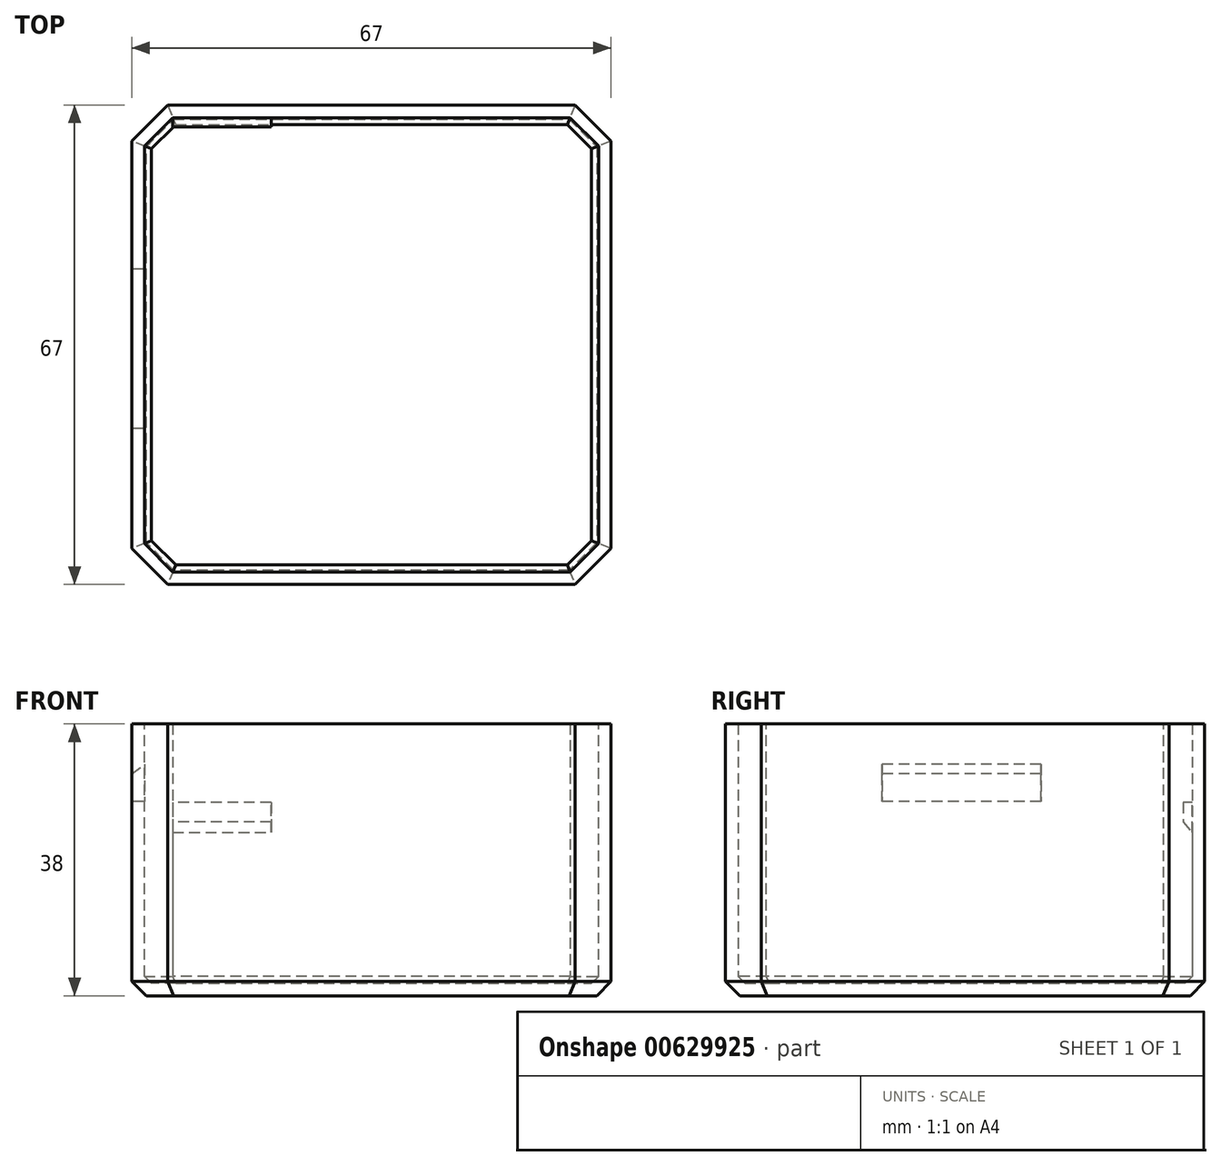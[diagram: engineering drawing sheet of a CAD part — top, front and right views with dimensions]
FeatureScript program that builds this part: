
annotation { "Feature Type Name" : "Feature", "Feature Type Description" : "" }
export const myFeature = defineFeature(function(context is Context, id is Id, definition is map)
    precondition{}
    {
        {
            var Q0;
            Q0=qCreatedBy(makeId("Top.planeOp"),FACE);
            var sketch = newSketch(context, id + "F0", { "sketchPlane" : qUnion([Q0])});
            skLineSegment(sketch, "E0.bottom", {"start": v(0, 0) * mm, "end": v(67, 0) * mm});
            skLineSegment(sketch, "E0.top", {"start": v(0, 67) * mm, "end": v(67, 67) * mm});
            skLineSegment(sketch, "E0.left", {"start": v(0, 0) * mm, "end": v(0, 67) * mm});
            skLineSegment(sketch, "E0.right", {"start": v(67, 0) * mm, "end": v(67, 67) * mm});
            skSolve(sketch);
        }
        {
            var Q0;
            Q0=makeQuery(id+"F0.imprint","IMPRINT",FACE,{"disambiguationData":[TD([[makeQuery(id+"F0.imprint","IMPRINT",EDGE,{"derivedFrom":sQuery(id+"F0.wireOp",EDGE,"E0.bottom")}),1.0]])]});
            extrude(context, id + "F1", {"entities" : qUnion([Q0]), "depth" : 38 * mm, "offsetDistance" : 25 * mm});
        }
        {
            var Q0;
            Q0=makeQuery(id+"F1.opExtrude","SWEPT_EDGE",EDGE,{"disambiguationData":[OSD([sQuery(id+"F0.wireOp",EDGE,"E0.top"),sQuery(id+"F0.wireOp",EDGE,"E0.right")])]});
            var Q1;
            Q1=makeQuery(id+"F1.opExtrude","SWEPT_EDGE",EDGE,{"disambiguationData":[OSD([sQuery(id+"F0.wireOp",EDGE,"E0.bottom"),sQuery(id+"F0.wireOp",EDGE,"E0.right")])]});
            var Q2;
            Q2=makeQuery(id+"F1.opExtrude","SWEPT_EDGE",EDGE,{"disambiguationData":[OSD([sQuery(id+"F0.wireOp",EDGE,"E0.bottom"),sQuery(id+"F0.wireOp",EDGE,"E0.left")])]});
            var Q3;
            Q3=makeQuery(id+"F1.opExtrude","SWEPT_EDGE",EDGE,{"disambiguationData":[OSD([sQuery(id+"F0.wireOp",EDGE,"E0.top"),sQuery(id+"F0.wireOp",EDGE,"E0.left")])]});
            chamfer(context, id + "F2", {"entities" : qUnion([Q0, Q1, Q2, Q3]), "width" : 5 * mm, "tangentPropagation" : true});
        }
        {
            var Q0;
            Q0=makeQuery(id+"F1.opExtrude","CAP_EDGE",EDGE,{"disambiguationData":[OSD([sQuery(id+"F0.wireOp",EDGE,"E0.left")])],"isStart":true});
            var Q1;
            Q1=makeQuery(id+"F1.opExtrude","CAP_EDGE",EDGE,{"disambiguationData":[OSD([sQuery(id+"F0.wireOp",EDGE,"E0.bottom")])],"isStart":true});
            var Q2;
            {var subQ0=sQuery(id+"F0.wireOp",EDGE,"E0.left");var subQ1=sQuery(id+"F0.wireOp",EDGE,"E0.bottom");Q2=makeQuery(id+"F2.opChamfer","BLEND_EDGE",EDGE,{"blendedFrom":[makeQuery(id+"F1.opExtrude","SWEPT_EDGE",EDGE,{"disambiguationData":[OSD([subQ1,subQ0])]}),makeQuery(id+"F1.opExtrude","CAP_FACE",FACE,{"disambiguationData":[OSD([subQ1,sQuery(id+"F0.wireOp",EDGE,"E0.top"),subQ0,sQuery(id+"F0.wireOp",EDGE,"E0.right")])],"isStart":true})],"blendedInto":[makeQuery(id+"F1.opExtrude","CAP_FACE",FACE,{"disambiguationData":[OSD([subQ1,sQuery(id+"F0.wireOp",EDGE,"E0.top"),subQ0,sQuery(id+"F0.wireOp",EDGE,"E0.right")])],"isStart":true})]});}
            var Q3;
            {var subQ0=sQuery(id+"F0.wireOp",EDGE,"E0.right");var subQ1=sQuery(id+"F0.wireOp",EDGE,"E0.bottom");Q3=makeQuery(id+"F2.opChamfer","BLEND_EDGE",EDGE,{"blendedFrom":[makeQuery(id+"F1.opExtrude","SWEPT_EDGE",EDGE,{"disambiguationData":[OSD([subQ1,subQ0])]}),makeQuery(id+"F1.opExtrude","CAP_FACE",FACE,{"disambiguationData":[OSD([subQ1,sQuery(id+"F0.wireOp",EDGE,"E0.top"),sQuery(id+"F0.wireOp",EDGE,"E0.left"),subQ0])],"isStart":true})],"blendedInto":[makeQuery(id+"F1.opExtrude","CAP_FACE",FACE,{"disambiguationData":[OSD([subQ1,sQuery(id+"F0.wireOp",EDGE,"E0.top"),sQuery(id+"F0.wireOp",EDGE,"E0.left"),subQ0])],"isStart":true})]});}
            var Q4;
            Q4=makeQuery(id+"F1.opExtrude","CAP_FACE",FACE,{"disambiguationData":[OSD([sQuery(id+"F0.wireOp",EDGE,"E0.bottom"),sQuery(id+"F0.wireOp",EDGE,"E0.top"),sQuery(id+"F0.wireOp",EDGE,"E0.left"),sQuery(id+"F0.wireOp",EDGE,"E0.right")])],"isStart":true});
            chamfer(context, id + "F3", {"entities" : qUnion([Q0, Q1, Q2, Q3, Q4]), "width" : 2 * mm, "tangentPropagation" : true});
        }
        {
            var Q0;
            Q0=makeQuery(id+"F1.opExtrude","CAP_FACE",FACE,{"disambiguationData":[OSD([sQuery(id+"F0.wireOp",EDGE,"E0.bottom"),sQuery(id+"F0.wireOp",EDGE,"E0.top"),sQuery(id+"F0.wireOp",EDGE,"E0.left"),sQuery(id+"F0.wireOp",EDGE,"E0.right")])],"isStart":false});
            shell(context, id + "F4", {"entities" : qUnion([Q0]), "thickness" : 1.75 * mm});
        }
        {
            var Q0;
            Q0=qCreatedBy(makeId("Front.planeOp"),FACE);
            cPlane(context, id + "F5", {"entities" : qUnion([Q0]), "cplaneType" : CPlaneType.OFFSET, "offset" : 21.87 * mm, "oppositeDirection" : true, "width" : 150 * mm, "height" : 150 * mm});
        }
        {
            var Q0;
            Q0=qCreatedBy(id+"F5.planeOp",FACE);
            var sketch = newSketch(context, id + "F6", { "sketchPlane" : qUnion([Q0])});
            skLineSegment(sketch, "E1", {"start": v(0, 31) * mm, "end": v(1.75, 32.36) * mm});
            skLineSegment(sketch, "E2", {"start": v(1.75, 32.36) * mm, "end": v(1.75, 27.14) * mm});
            skLineSegment(sketch, "E3", {"start": v(1.75, 27.14) * mm, "end": v(0, 27.14) * mm});
            skLineSegment(sketch, "E4", {"start": v(0, 27.14) * mm, "end": v(0, 31) * mm});
            skSolve(sketch);
        }
        {
            var Q0;
            Q0 = qSketchRegion(id + "F6", true);
            extrude(context, id + "F7", {"entities" : qUnion([Q0]), "operationType" : NewBodyOperationType.REMOVE, "oppositeDirection" : true, "depth" : 22.26 * mm, "offsetDistance" : 25 * mm});
        }
        {
            var Q0;
            Q0=makeQuery(id+"F1.opExtrude","SWEPT_FACE",FACE,{"disambiguationData":[OSD([sQuery(id+"F0.wireOp",EDGE,"E0.left")])]});
            var Q1;
            Q1=makeQuery(id+"F1.opExtrude","SWEPT_FACE",FACE,{"disambiguationData":[OSD([sQuery(id+"F0.wireOp",EDGE,"E0.right")])]});
            cPlane(context, id + "F8", {"entities" : qUnion([Q0, Q1]), "cplaneType" : CPlaneType.MID_PLANE, "offset" : 25 * mm, "width" : 150 * mm, "height" : 150 * mm});
        }
        {
            var Q0;
            {var subQ0=sQuery(id+"F0.wireOp",EDGE,"E0.top");var subQ1=sQuery(id+"F0.wireOp",EDGE,"E0.left");Q0=makeQuery(id+"F4.opShell","OFFSET_EDGE",EDGE,{"disambiguationData":[OSD([subQ0,subQ1]),TDD([makeQuery(id+"F2.opChamfer","BLEND_EDGE",EDGE,{"blendedFrom":[makeQuery(id+"F1.opExtrude","SWEPT_EDGE",EDGE,{"disambiguationData":[OSD([subQ0,subQ1])]}),makeQuery(id+"F1.opExtrude","SWEPT_FACE",FACE,{"disambiguationData":[OSD([subQ0])]})],"blendedInto":[makeQuery(id+"F1.opExtrude","SWEPT_FACE",FACE,{"disambiguationData":[OSD([subQ0])]})]})])]});}
            cPlane(context, id + "F9", {"entities" : qUnion([Q0]), "cplaneType" : CPlaneType.LINE_ANGLE, "offset" : 25 * mm, "angle" : 0 * degree, "width" : 150 * mm, "height" : 150 * mm});
        }
        {
            var Q0;
            Q0=qCreatedBy(id+"F9.planeOp",FACE);
            var sketch = newSketch(context, id + "F10", { "sketchPlane" : qUnion([Q0])});
            skLineSegment(sketch, "E5", {"start": v(-65.97, 27) * mm, "end": v(-63.97, 27) * mm});
            skLineSegment(sketch, "E6", {"start": v(-63.97, 27) * mm, "end": v(-63.97, 24.3) * mm});
            skLineSegment(sketch, "E7", {"start": v(-63.97, 24.3) * mm, "end": v(-65.97, 22) * mm});
            skLineSegment(sketch, "E8", {"start": v(-65.97, 22) * mm, "end": v(-65.97, 27) * mm});
            skSolve(sketch);
        }
        {
            var Q0;
            Q0=makeQuery(id+"F10.imprint","IMPRINT",FACE,{"disambiguationData":[TD([[makeQuery(id+"F10.imprint","IMPRINT",EDGE,{"derivedFrom":sQuery(id+"F10.wireOp",EDGE,"E5")}),-1.0]])]});
            extrude(context, id + "F11", {"entities" : qUnion([Q0]), "operationType" : NewBodyOperationType.ADD, "oppositeDirection" : true, "depth" : 13.75 * mm, "offsetDistance" : 25 * mm});
        }
        {
            var Q0;
            Q0=makeQuery(id+"F1.opExtrude","SWEPT_FACE",FACE,{"disambiguationData":[OSD([sQuery(id+"F0.wireOp",EDGE,"E0.bottom")])]});
            var Q1;
            Q1=makeQuery(id+"F1.opExtrude","SWEPT_FACE",FACE,{"disambiguationData":[OSD([sQuery(id+"F0.wireOp",EDGE,"E0.top")])]});
            cPlane(context, id + "F12", {"entities" : qUnion([Q0, Q1]), "cplaneType" : CPlaneType.MID_PLANE, "offset" : 25 * mm, "width" : 150 * mm, "height" : 150 * mm});
        }
    });
